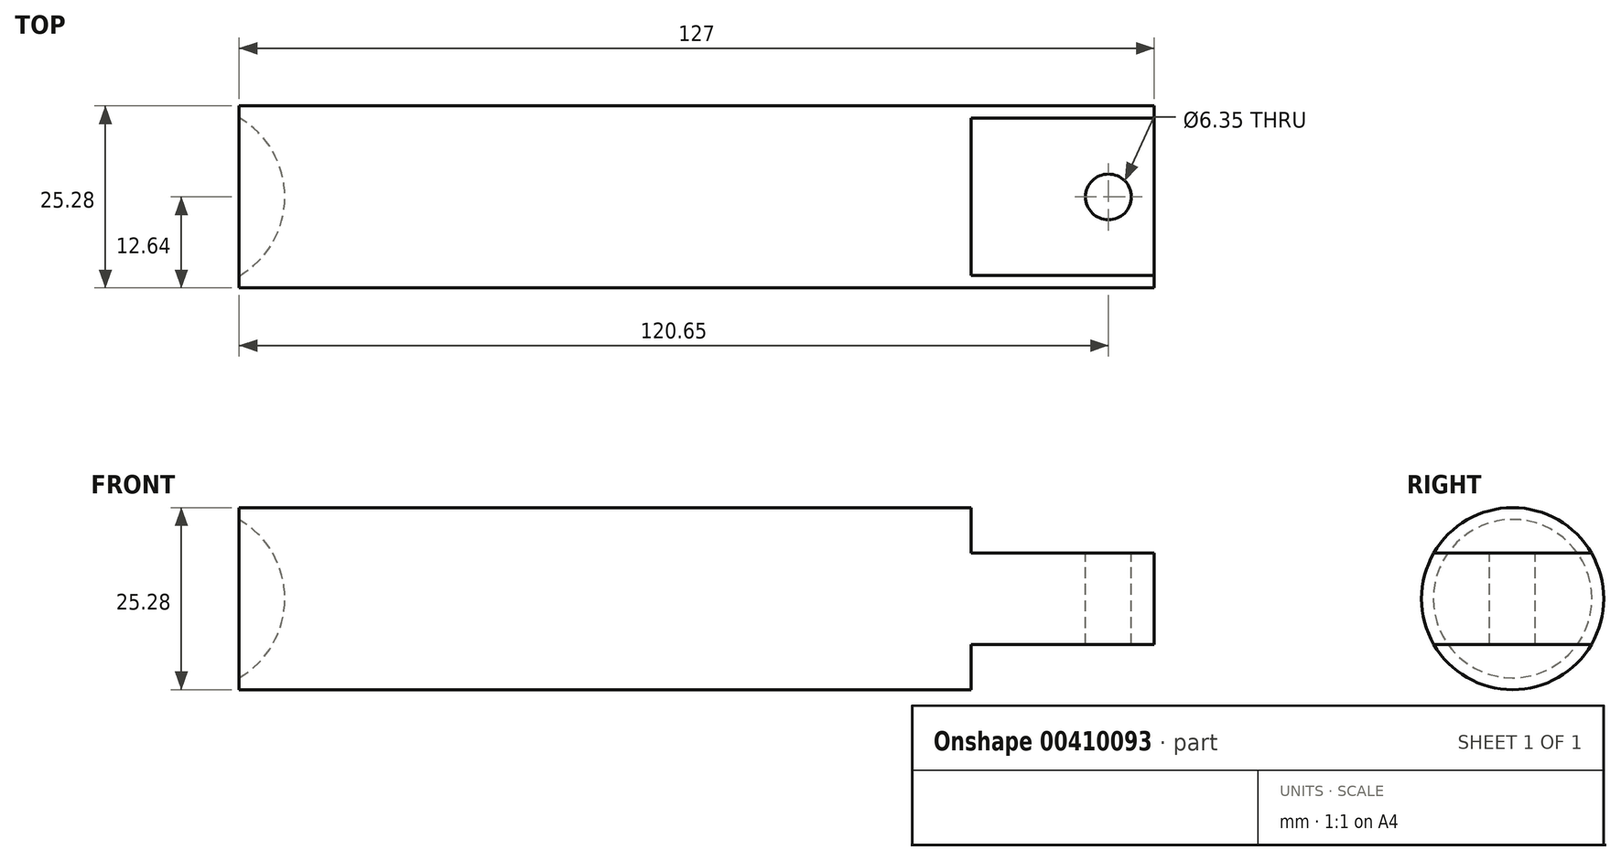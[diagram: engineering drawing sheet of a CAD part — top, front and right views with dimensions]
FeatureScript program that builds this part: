
annotation { "Feature Type Name" : "Feature", "Feature Type Description" : "" }
export const myFeature = defineFeature(function(context is Context, id is Id, definition is map)
    precondition{}
    {
        {
            var Q0;
            Q0=qCreatedBy(makeId("Right.planeOp"),FACE);
            var sketch = newSketch(context, id + "F0", { "sketchPlane" : qUnion([Q0])});
            skCircle(sketch, "E0", {"center": v(0, 0) * mm, "radius": 12.64 * mm});
            skSolve(sketch);
        }
        {
            var Q0;
            Q0=makeQuery(id+"F0.imprint","IMPRINT",FACE,{"disambiguationData":[TD([[makeQuery(id+"F0.imprint","IMPRINT",EDGE,{"derivedFrom":sQuery(id+"F0.wireOp",EDGE,"E0")}),1.0]])]});
            extrude(context, id + "F1", {"entities" : qUnion([Q0]), "depth" : 127 * mm});
        }
        {
            var Q0;
            Q0=qCreatedBy(makeId("Front.planeOp"),FACE);
            var sketch = newSketch(context, id + "F2", { "sketchPlane" : qUnion([Q0])});
            skLineSegment(sketch, "E1", {"start": v(0, 12.64) * mm, "end": v(101.6, 12.64) * mm});
            skLineSegment(sketch, "E2", {"start": v(101.6, -12.64) * mm, "end": v(0, -12.64) * mm});
            skLineSegment(sketch, "E3", {"start": v(-6.35, 12.7) * mm, "end": v(-6.35, -12.7) * mm});
            skArc(sketch, "E4", {"start": v(-6.35, -12.7) * mm, "mid": v(6.35, 0) * mm, "end": v(-6.35, 12.7) * mm});
            skSolve(sketch);
        }
        {
            var Q0;
            Q0=makeQuery(id+"F2.imprint","IMPRINT",FACE,{"disambiguationData":[TD([[makeQuery(id+"F2.imprint","IMPRINT",EDGE,{"derivedFrom":sQuery(id+"F2.wireOp",EDGE,"E3")}),1.0]])]});
            var Q1;
            Q1=sQuery(id+"F2.wireOp",EDGE,"E3");
            revolve(context, id + "F3", {"operationType" : NewBodyOperationType.REMOVE, "entities" : qUnion([Q0]), "axis" : qUnion([Q1]), "revolveType" : RevolveType.FULL, "oppositeDirection" : true});
        }
        {
            var Q0;
            Q0=qCreatedBy(makeId("Front.planeOp"),FACE);
            var sketch = newSketch(context, id + "F4", { "sketchPlane" : qUnion([Q0])});
            skLineSegment(sketch, "E5", {"start": v(0, 12.64) * mm, "end": v(127, 12.64) * mm});
            skLineSegment(sketch, "E6", {"start": v(127, -12.64) * mm, "end": v(0, -12.64) * mm});
            skLineSegment(sketch, "E7.bottom", {"start": v(132.32, 17.1) * mm, "end": v(101.6, 17.1) * mm});
            skLineSegment(sketch, "E7.top", {"start": v(132.32, 6.35) * mm, "end": v(101.6, 6.35) * mm});
            skLineSegment(sketch, "E7.left", {"start": v(132.32, 17.1) * mm, "end": v(132.32, 6.35) * mm});
            skLineSegment(sketch, "E7.right", {"start": v(101.6, 17.1) * mm, "end": v(101.6, 6.35) * mm});
            skLineSegment(sketch, "E8.bottom", {"start": v(101.6, -6.35) * mm, "end": v(140.87, -6.35) * mm});
            skLineSegment(sketch, "E8.top", {"start": v(101.6, -25.53) * mm, "end": v(140.87, -25.53) * mm});
            skLineSegment(sketch, "E8.left", {"start": v(101.6, -6.35) * mm, "end": v(101.6, -25.53) * mm});
            skLineSegment(sketch, "E8.right", {"start": v(140.87, -6.35) * mm, "end": v(140.87, -25.53) * mm});
            skLineSegment(sketch, "E9", {"start": v(0, 0) * mm, "end": v(158.28, 0) * mm});
            skSolve(sketch);
        }
        {
            var Q0;
            Q0 = qSketchRegion(id + "F4", true);
            extrude(context, id + "F5", {"entities" : qUnion([Q0]), "operationType" : NewBodyOperationType.REMOVE, "depth" : 25.4 * mm});
        }
        {
            var Q0;
            {var subQ3=sQuery(id+"F4.wireOp",EDGE,"E8.bottom");Q0=makeQuery(id+"F4.imprint","IMPRINT",FACE,{"disambiguationData":[TD([[makeQuery(id+"F4.imprint","IMPRINT",EDGE,{"derivedFrom":subQ3}),-1.0]])]});}
            var Q1;
            {var subQ1=sQuery(id+"F4.wireOp",EDGE,"E7.bottom");Q1=makeQuery(id+"F4.imprint","IMPRINT",FACE,{"disambiguationData":[TD([[makeQuery(id+"F4.imprint","IMPRINT",EDGE,{"derivedFrom":subQ1}),1.0]])]});}
            extrude(context, id + "F6", {"entities" : qUnion([Q0, Q1]), "operationType" : NewBodyOperationType.REMOVE, "oppositeDirection" : true, "depth" : 25.4 * mm});
        }
        {
            var Q0;
            {var subQ0=sQuery(id+"F4.wireOp",EDGE,"E7.top");Q0=makeQuery(id+"F6.boolean.opBoolean","MERGE",FACE,{"derivedFrom":[makeQuery(id+"F5.boolean.opBoolean","COPY",FACE,{"derivedFrom":makeQuery(id+"F5.opExtrude","SWEPT_FACE",FACE,{"disambiguationData":[OSD([subQ0])]})}),makeQuery(id+"F6.opExtrude","SWEPT_FACE",FACE,{"disambiguationData":[OSD([subQ0])]})]});}
            var sketch = newSketch(context, id + "F7", { "sketchPlane" : qUnion([Q0])});
            skLineSegment(sketch, "E10.0.0", {"start": v(127, -10.93) * mm, "end": v(127, 10.93) * mm});
            skLineSegment(sketch, "E10.0.1", {"start": v(127, 10.93) * mm, "end": v(101.6, 10.93) * mm});
            skLineSegment(sketch, "E10.0.2", {"start": v(101.6, 10.93) * mm, "end": v(101.6, -10.93) * mm});
            skLineSegment(sketch, "E10.0.3", {"start": v(101.6, -10.93) * mm, "end": v(127, -10.93) * mm});
            skCircle(sketch, "E11", {"center": v(120.65, 0) * mm, "radius": 3.18 * mm});
            skSolve(sketch);
        }
        {
            var Q0;
            Q0=makeQuery(id+"F7.imprint","IMPRINT",FACE,{"disambiguationData":[TD([[makeQuery(id+"F7.imprint","IMPRINT",EDGE,{"derivedFrom":sQuery(id+"F7.wireOp",EDGE,"E11")}),1.0]])]});
            extrude(context, id + "F8", {"entities" : qUnion([Q0]), "operationType" : NewBodyOperationType.REMOVE, "endBound" : BoundingType.THROUGH_ALL, "oppositeDirection" : true, "depth" : 25.4 * mm});
        }
    });
